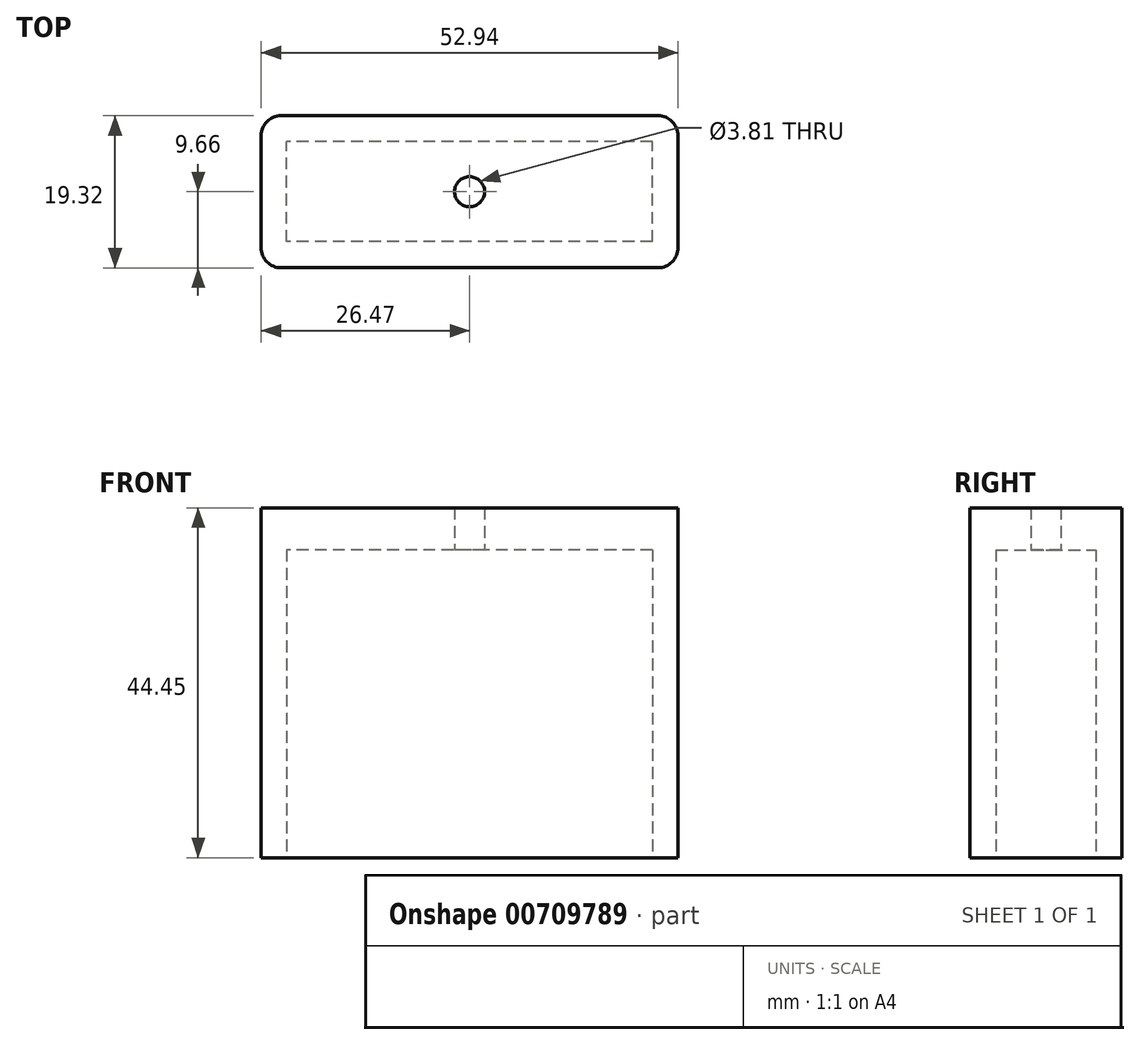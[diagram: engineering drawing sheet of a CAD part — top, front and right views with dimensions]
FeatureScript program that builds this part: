
annotation { "Feature Type Name" : "Feature", "Feature Type Description" : "" }
export const myFeature = defineFeature(function(context is Context, id is Id, definition is map)
    precondition{}
    {
        {
            var Q0;
            Q0=qCreatedBy(makeId("Top.planeOp"),FACE);
            var sketch = newSketch(context, id + "F0", { "sketchPlane" : qUnion([Q0])});
            skLineSegment(sketch, "E0.bottom", {"start": v(-23.24, 6.35) * mm, "end": v(23.24, 6.35) * mm});
            skLineSegment(sketch, "E0.top", {"start": v(-23.24, -6.35) * mm, "end": v(23.24, -6.35) * mm});
            skLineSegment(sketch, "E0.left", {"start": v(-23.24, 6.35) * mm, "end": v(-23.24, -6.35) * mm});
            skLineSegment(sketch, "E0.right", {"start": v(23.24, 6.35) * mm, "end": v(23.24, -6.35) * mm});
            skPoint(sketch, "E0.middle", {"position": v(0, 0) * mm});
            skLineSegment(sketch, "E1.bottom", {"start": v(-26.47, 9.66) * mm, "end": v(26.47, 9.66) * mm});
            skLineSegment(sketch, "E1.top", {"start": v(-26.47, -9.66) * mm, "end": v(26.47, -9.66) * mm});
            skLineSegment(sketch, "E1.left", {"start": v(-26.47, 9.66) * mm, "end": v(-26.47, -9.66) * mm});
            skLineSegment(sketch, "E1.right", {"start": v(26.47, 9.66) * mm, "end": v(26.47, -9.66) * mm});
            skSolve(sketch);
        }
        {
            var Q0;
            Q0=makeQuery(id+"F0.imprint","IMPRINT",FACE,{"disambiguationData":[TD([[makeQuery(id+"F0.imprint","IMPRINT",EDGE,{"derivedFrom":sQuery(id+"F0.wireOp",EDGE,"E0.bottom")}),1.0]])]});
            var Q1;
            Q1=makeQuery(id+"F0.imprint","IMPRINT",FACE,{"disambiguationData":[TD([[makeQuery(id+"F0.imprint","IMPRINT",EDGE,{"derivedFrom":sQuery(id+"F0.wireOp",EDGE,"E0.bottom")}),-1.0]])]});
            extrude(context, id + "F1", {"entities" : qUnion([Q0, Q1]), "depth" : 44.45 * mm, "offsetDistance" : 25.4 * mm});
        }
        {
            var Q0;
            Q0=qCreatedBy(makeId("Top.planeOp"),FACE);
            var sketch = newSketch(context, id + "F2", { "sketchPlane" : qUnion([Q0])});
            skLineSegment(sketch, "E2.bottom", {"start": v(23.24, -6.35) * mm, "end": v(-23.24, -6.35) * mm});
            skLineSegment(sketch, "E2.top", {"start": v(23.24, 6.35) * mm, "end": v(-23.24, 6.35) * mm});
            skLineSegment(sketch, "E2.left", {"start": v(23.24, -6.35) * mm, "end": v(23.24, 6.35) * mm});
            skLineSegment(sketch, "E2.right", {"start": v(-23.24, -6.35) * mm, "end": v(-23.24, 6.35) * mm});
            skPoint(sketch, "E2.middle", {"position": v(0, 0) * mm});
            skSolve(sketch);
        }
        {
            var Q0;
            Q0=makeQuery(id+"F2.imprint","IMPRINT",FACE,{"disambiguationData":[TD([[makeQuery(id+"F2.imprint","IMPRINT",EDGE,{"derivedFrom":sQuery(id+"F2.wireOp",EDGE,"E2.bottom")}),-1.0]])]});
            extrude(context, id + "F3", {"entities" : qUnion([Q0]), "operationType" : NewBodyOperationType.REMOVE, "depth" : 39.12 * mm, "offsetDistance" : 25.4 * mm});
        }
        {
            var Q0;
            Q0=qCreatedBy(makeId("Top.planeOp"),FACE);
            var sketch = newSketch(context, id + "F4", { "sketchPlane" : qUnion([Q0])});
            skCircle(sketch, "E3", {"center": v(0, 0) * mm, "radius": 1.9 * mm});
            skSolve(sketch);
        }
        {
            var Q0;
            Q0=makeQuery(id+"F4.imprint","IMPRINT",FACE,{"disambiguationData":[TD([[makeQuery(id+"F4.imprint","IMPRINT",EDGE,{"derivedFrom":sQuery(id+"F4.wireOp",EDGE,"E3")}),1.0]])]});
            extrude(context, id + "F5", {"entities" : qUnion([Q0]), "operationType" : NewBodyOperationType.REMOVE, "depth" : 58.67 * mm, "offsetDistance" : 25.4 * mm});
        }
        {
            var Q0;
            Q0=makeQuery(id+"F1.opExtrude","SWEPT_EDGE",EDGE,{"disambiguationData":[OSD([sQuery(id+"F0.wireOp",EDGE,"E1.bottom"),sQuery(id+"F0.wireOp",EDGE,"E1.left")])]});
            var Q1;
            Q1=makeQuery(id+"F1.opExtrude","SWEPT_EDGE",EDGE,{"disambiguationData":[OSD([sQuery(id+"F0.wireOp",EDGE,"E1.bottom"),sQuery(id+"F0.wireOp",EDGE,"E1.right")])]});
            var Q2;
            Q2=makeQuery(id+"F1.opExtrude","SWEPT_EDGE",EDGE,{"disambiguationData":[OSD([sQuery(id+"F0.wireOp",EDGE,"E1.top"),sQuery(id+"F0.wireOp",EDGE,"E1.left")])]});
            var Q3;
            Q3=makeQuery(id+"F1.opExtrude","SWEPT_EDGE",EDGE,{"disambiguationData":[OSD([sQuery(id+"F0.wireOp",EDGE,"E1.top"),sQuery(id+"F0.wireOp",EDGE,"E1.right")])]});
            fillet(context, id + "F6", {"entities" : qUnion([Q0, Q1, Q2, Q3]), "radius" : 2.54 * mm, "tangentPropagation" : true, "allowEdgeOverflow" : false});
        }
    });
